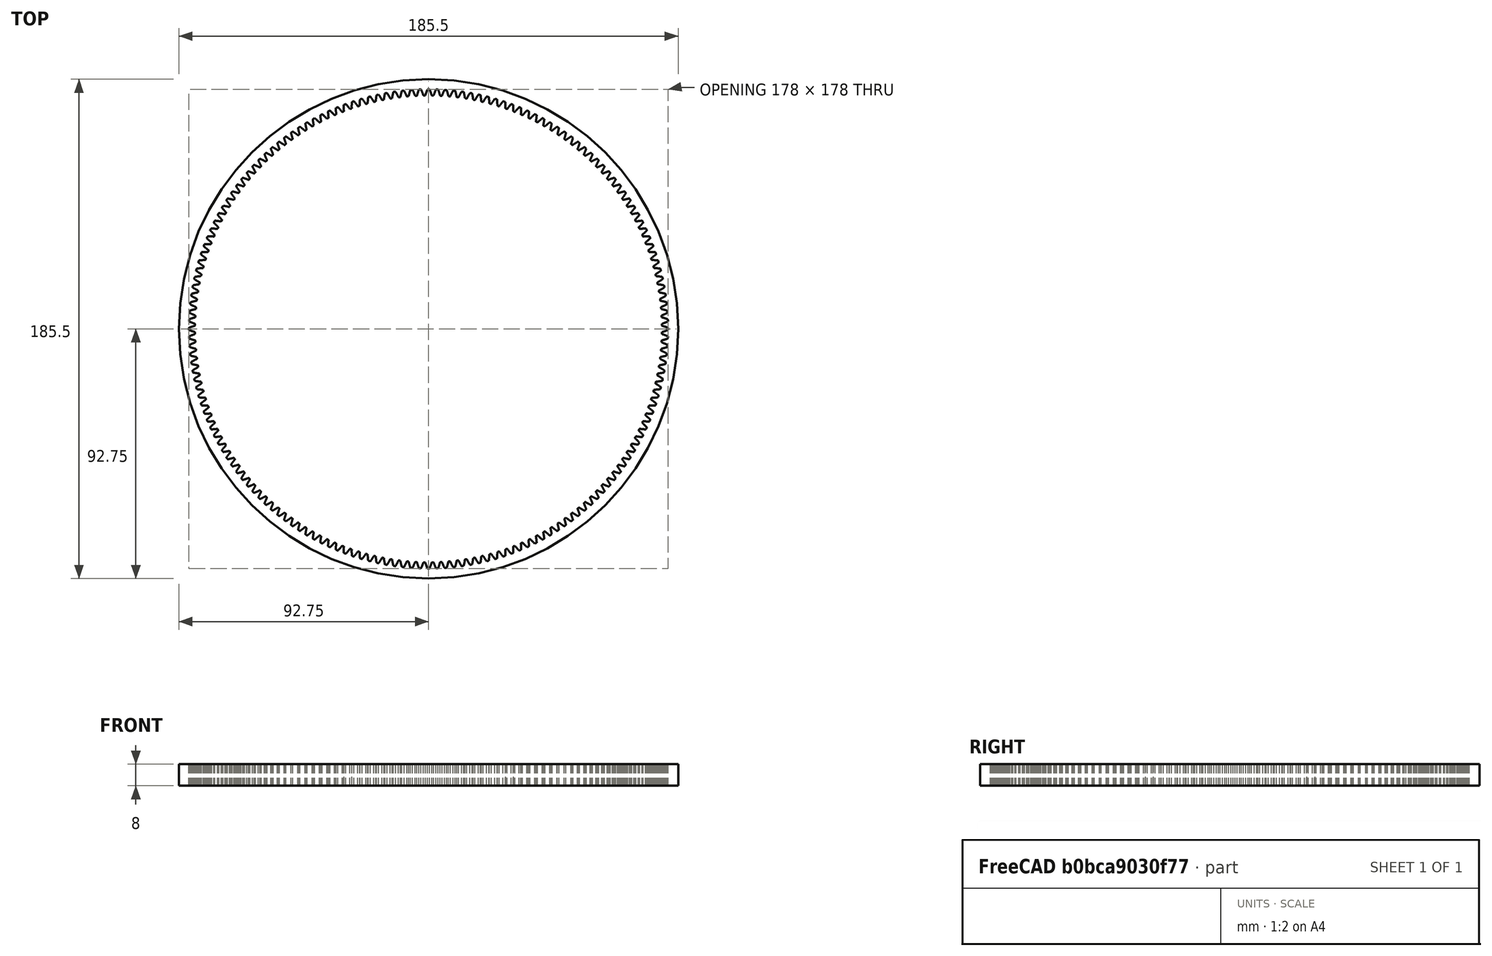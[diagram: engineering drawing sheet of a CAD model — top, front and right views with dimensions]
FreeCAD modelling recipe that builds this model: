
FCSTD DOCUMENT  (FreeCAD 0.19R24276 (Git))
Label: Out_gear_t176_d185_5
License: All rights reserved
LicenseURL: http://en.wikipedia.org/wiki/All_rights_reserved
objects: Part::FeaturePython×1, Part::Cylinder×1, Part::Cut×1
note: 3 computed .brp shape members not serialized (recipe doc carries the construction recipe); baked Part::Feature solids carry a one-line shape summary decoded from their .brp

FEATURE [Part::FeaturePython] involutegear  # WARN: FeaturePython — macro-defined, semantics opaque (R4)
  AttacherType = Attacher::AttachEngine3D
  backlash = 0
  beta = 0
  clearance = 0.25
  da = 178
  df = 173.5
  double_helix = false
  dw = 176
  head = 0
  height = 8
  module = 1
  numpoints = 6
  pressure_angle = 20
  properties_from_tool = false
  reversed_backlash = false
  shift = 0
  simple = false
  teeth = 176
  transverse_pitch = 3.14159
  undercut = false
  version = 0.0.3
FEATURE [Part::Cylinder] Cylinder  label="Цилиндр"
  Angle = 360
  AttacherType = Attacher::AttachEngine3D
  Height = 8
  Radius = 92.75
FEATURE [Part::Cut] Cut
  Base = -> Cylinder
  Tool = -> involutegear
